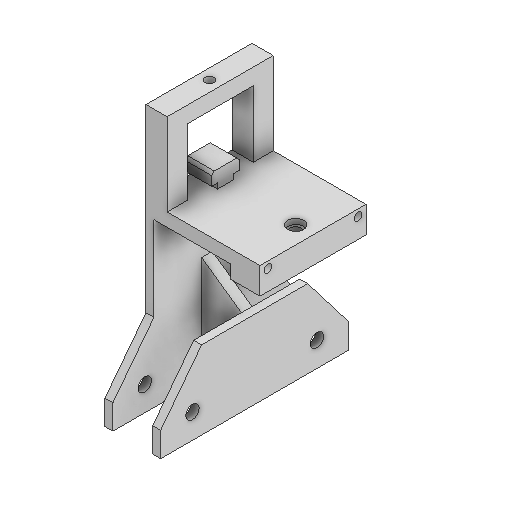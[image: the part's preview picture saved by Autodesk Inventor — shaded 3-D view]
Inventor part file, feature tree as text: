
AUTODESK INVENTOR PART (.ipt)
format: ipt  version: 2025.1 (Build 291241000, 241)  size: 259,584 bytes
history: native  units: mm
features: sketch x14, extrude x10, hole x4, other x1, chamfer x1
ambient origin geometry x8: Origin, YZ Plane, XZ Plane, XY Plane, X Axis, Y Axis, Z Axis, Center Point
bodies: Body1 (feature_tree)
feature tree (30):
  other  "Bryła1"
  extrude  "Wyciągnięcie proste1"  Depth=25.0mm
  hole  "Otwór1"  [1 undecoded]
  extrude  "Wyciągnięcie proste2"  Depth=82.089mm
  extrude  "Wyciągnięcie proste3"  Depth=20.0mm
  extrude  "Wyciągnięcie proste4"  Depth=3.0mm TaperAngle=0.0deg
  chamfer  "Faza1"  Distance=82.089mm
  extrude  "Wyciągnięcie proste5"  Depth=82.089mm
  hole  "Otwór3"  [1 undecoded]
  extrude  "Wyciągnięcie proste6"  Depth=12.0mm
  extrude  "Wyciągnięcie proste7"  Depth=5.0mm TaperAngle=0.0deg
  hole  "Otwór4"  [1 undecoded]
  extrude  "Wyciągnięcie proste8"  Depth=40.0mm
  extrude  "Wyciągnięcie proste9"  Depth=4.0mm
  extrude  "Wyciągnięcie proste10"  Depth=15.0mm TaperAngle=0.0deg
  hole  "Otwór5"  [1 undecoded]
  sketch  "Szkic1"
  sketch  "Szkic2"
  sketch  "Szkic3"
  sketch  "Szkic5"
  sketch  "Szkic6"
  sketch  "Szkic7"
  sketch  "Szkic8"
  sketch  "Szkic9"
  sketch  "Szkic10"
  sketch  "Szkic11"
  sketch  "Szkic13"
  sketch  "Szkic14"
  sketch  "Szkic15"
  sketch  "Szkic16"
note: 4 required parameter values undecoded (feature->parameter linkage not recoverable at this tier; creation-order binding heuristic only, values carry confidence <= 0.55)
